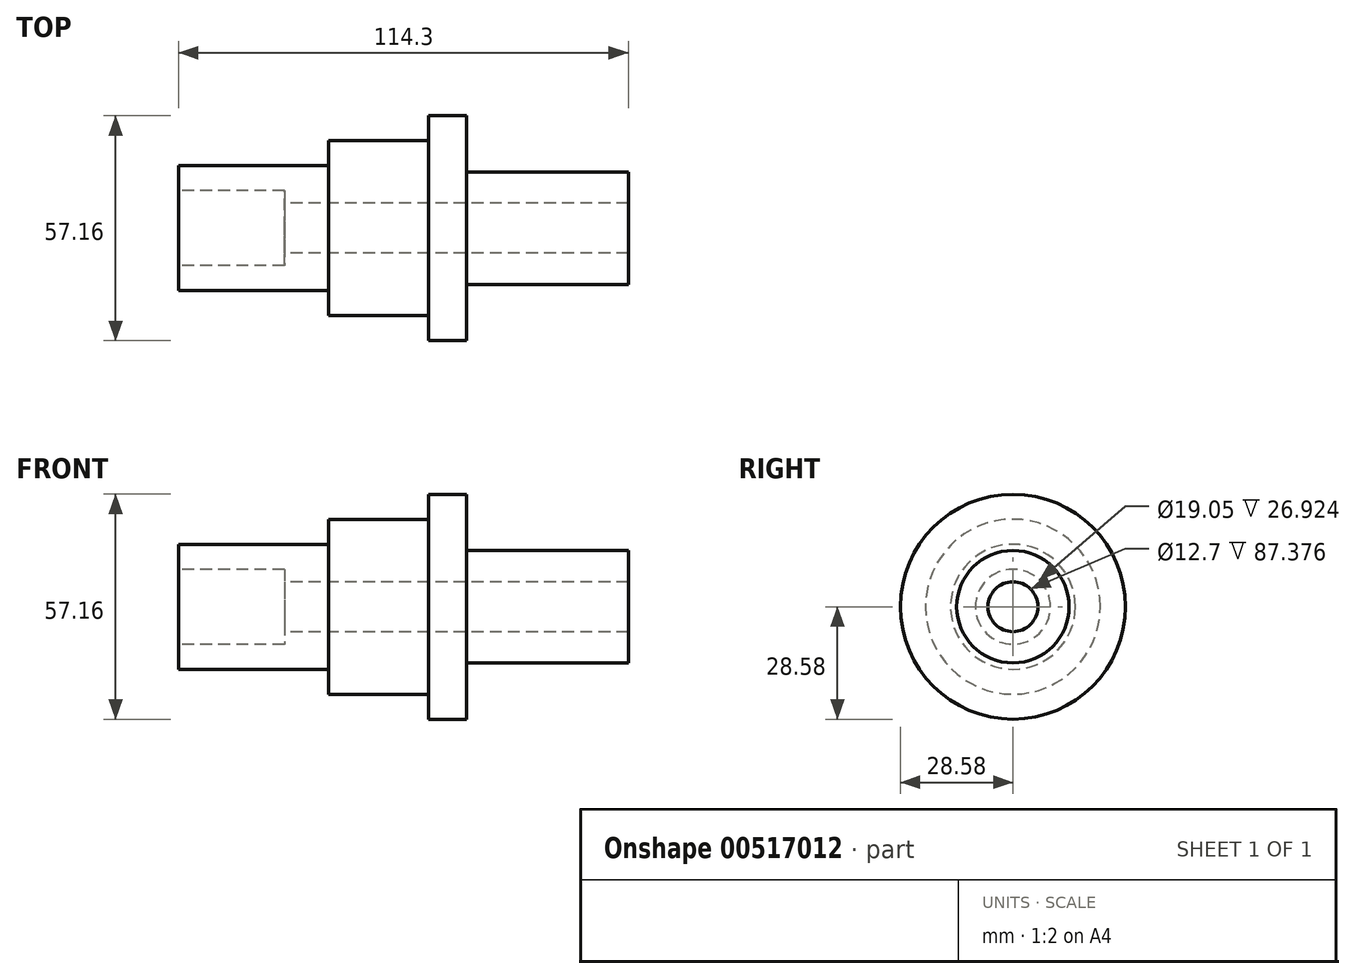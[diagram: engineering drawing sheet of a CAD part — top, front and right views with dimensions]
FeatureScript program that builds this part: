
annotation { "Feature Type Name" : "Feature", "Feature Type Description" : "" }
export const myFeature = defineFeature(function(context is Context, id is Id, definition is map)
    precondition{}
    {
        {
            var Q0;
            Q0=qCreatedBy(makeId("Front.planeOp"),FACE);
            var sketch = newSketch(context, id + "F0", { "sketchPlane" : qUnion([Q0])});
            skLineSegment(sketch, "E0", {"start": v(-112.48, 0) * mm, "end": v(114.13, 0) * mm, "construction": true});
            skPoint(sketch, "E1", {"position": v(0, 0) * mm});
            skLineSegment(sketch, "E2", {"start": v(-73.15, 9.53) * mm, "end": v(-73.15, 15.88) * mm});
            skLineSegment(sketch, "E3", {"start": v(-73.15, 15.88) * mm, "end": v(-35.05, 15.88) * mm});
            skLineSegment(sketch, "E4", {"start": v(-35.05, 15.88) * mm, "end": v(-35.05, 22.23) * mm});
            skLineSegment(sketch, "E5", {"start": v(-35.05, 22.23) * mm, "end": v(-9.65, 22.23) * mm});
            skLineSegment(sketch, "E6", {"start": v(-9.65, 22.23) * mm, "end": v(-9.65, 28.58) * mm});
            skLineSegment(sketch, "E7", {"start": v(-9.65, 28.58) * mm, "end": v(0, 28.58) * mm});
            skLineSegment(sketch, "E8", {"start": v(0, 28.58) * mm, "end": v(0, 14.29) * mm});
            skLineSegment(sketch, "E9", {"start": v(0, 14.29) * mm, "end": v(41.15, 14.29) * mm});
            skLineSegment(sketch, "E10", {"start": v(41.15, 14.29) * mm, "end": v(41.15, 6.35) * mm});
            skLineSegment(sketch, "E11", {"start": v(41.15, 6.35) * mm, "end": v(-46.23, 6.35) * mm});
            skLineSegment(sketch, "E12", {"start": v(-46.23, 6.35) * mm, "end": v(-46.23, 9.53) * mm});
            skLineSegment(sketch, "E13", {"start": v(-46.23, 9.53) * mm, "end": v(-73.15, 9.53) * mm});
            skSolve(sketch);
        }
        {
            var Q0;
            Q0=makeQuery(id+"F0.imprint","IMPRINT",FACE,{"disambiguationData":[TD([[makeQuery(id+"F0.imprint","IMPRINT",EDGE,{"derivedFrom":sQuery(id+"F0.wireOp",EDGE,"E2")}),-1.0]])]});
            var Q1;
            Q1=sQuery(id+"F0.wireOp",EDGE,"E0");
            revolve(context, id + "F1", {"entities" : qUnion([Q0]), "axis" : qUnion([Q1]), "revolveType" : RevolveType.FULL});
        }
    });
